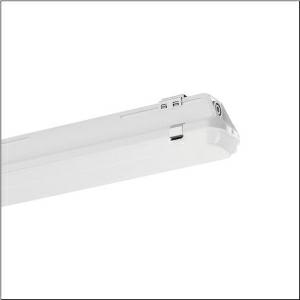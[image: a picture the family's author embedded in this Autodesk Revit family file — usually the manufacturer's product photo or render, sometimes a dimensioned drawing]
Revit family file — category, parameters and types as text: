
# Revit family: monsun_21_51fb10mp380c
name_source: partatom
category: Lighting Fixtures
units: mm (PartAtom-declared; Revit-internal decimal feet)

## family parameters
Cut with Voids When Loaded = No
Host = Face
Light Source = No
Part Type = Normal
Room Calculation Point = No
Round Connector Dimension = Use Diameter
Shared = No

## types (1)
- --- (1 x LED, 8490 lm, 49.1 W, 3000K)
    Apparent Load = 49 VA
    CIE Flux Codes = 47 77 93 94 100
    Color Rendering = 80
    Color Temperature = 3000K
    Default Elevation = 1800 mm
    Description = Monsun 21, damp-proof luminaire, chain hanger, primary optical cover: enclosure, of PMMA, light emission: direct distribution, primary light characteristic: symmetric, installation type: suspended mounting, surface-mounted, horizontal mounting, vertical mounting, LED, rated luminous flux: 8.490lm, luminous efficacy: 173lm/W, light colour: 830, colour temperature: 3000K, control gear: ON/OFF Multilumen, with terminal, 3-pole, max. 2.5mm², mains connection: 220..240V, AC, 50/60Hz, rated input power: 49W, housing, of glass-fibre reinforced polyester, uncoated, bright grey, incl. chain hanger, length: 1.590mm, width: 90mm, height: 88mm, clip for enclosure, of stainless steel (V2A), ceiling mounting element, of stainless steel (V2A), chain hanger, of stainless steel (V2A), protection rating (complete): IP66, insulation class (complete): insulation class I (protective earthing), certification: CE, ENEC, VDE, UKCA, protection symbol: D, impact resistance: IK04, permissible operating ambient temperature: -25..+35°C, standard: EN 50419, EN 60598-2-1, corresponds to IFS (International Featured Standards) requirements for safety and quality in the food industry, for indoor or canopied outdoor use, no direct snow, no direct sun, no direct rain, LABS conformity tested according to VDMA 24364:2018-05, contact your sales advisor before using the luminaires in applications with unclear chemical exposure, large temperature fluctuations or condensation-forming humidity, packaging unit: 1 piece
    Height = 89 mm
    Lamp = 1 x LED
    Lamp Light Flux = 8490 lm
    Lamp Power = 49.1 W
    Lamp count = 1
    Length = 1590 mm
    Luminous efficacy = 173 lm/W
    Manufacturer = Siteco
    ModVariant = No
    Model = 51FB10MP380C
    Mounting Place = Ceiling
    Mounting Type = Surface mounted
    Number of Poles = 1
    OnlyDefault = Yes
    Power Factor = 1
    Product Name = Monsun 21
    Product group = damp-proof luminaire
    ProductGroupID = 300
    Protection Class = Protection class I
    Protection Degree = IP 66
    RLX_Detail_Level = 1
    RLX_Emergency_Light_Flux = 0 lm
    RLX_Emergency_Type = 0
    RLX_Emergency_Type_DB = No
    RlxData = <blob elided: 90437 chars, md5=7d69c80a>
    Socket = socket
    Standby Power = 0 W
    System Light Flux = 8490 lm
    System Power = 49 W
    Type Comments = factory setting: luminous flux: 100 % | (A | C | E) | 114 mA
    Type Image = l_1319656.jpg
    URL = http://relux.com
    VarID = @adj_038413
    Voltage = 0 V
    Weight = 0.00 kg
    Width = 90 mm

## geometry (parser evidence)
native form markers: Blend x4, Sweep x11
no freeform markers — native parametric forms only
